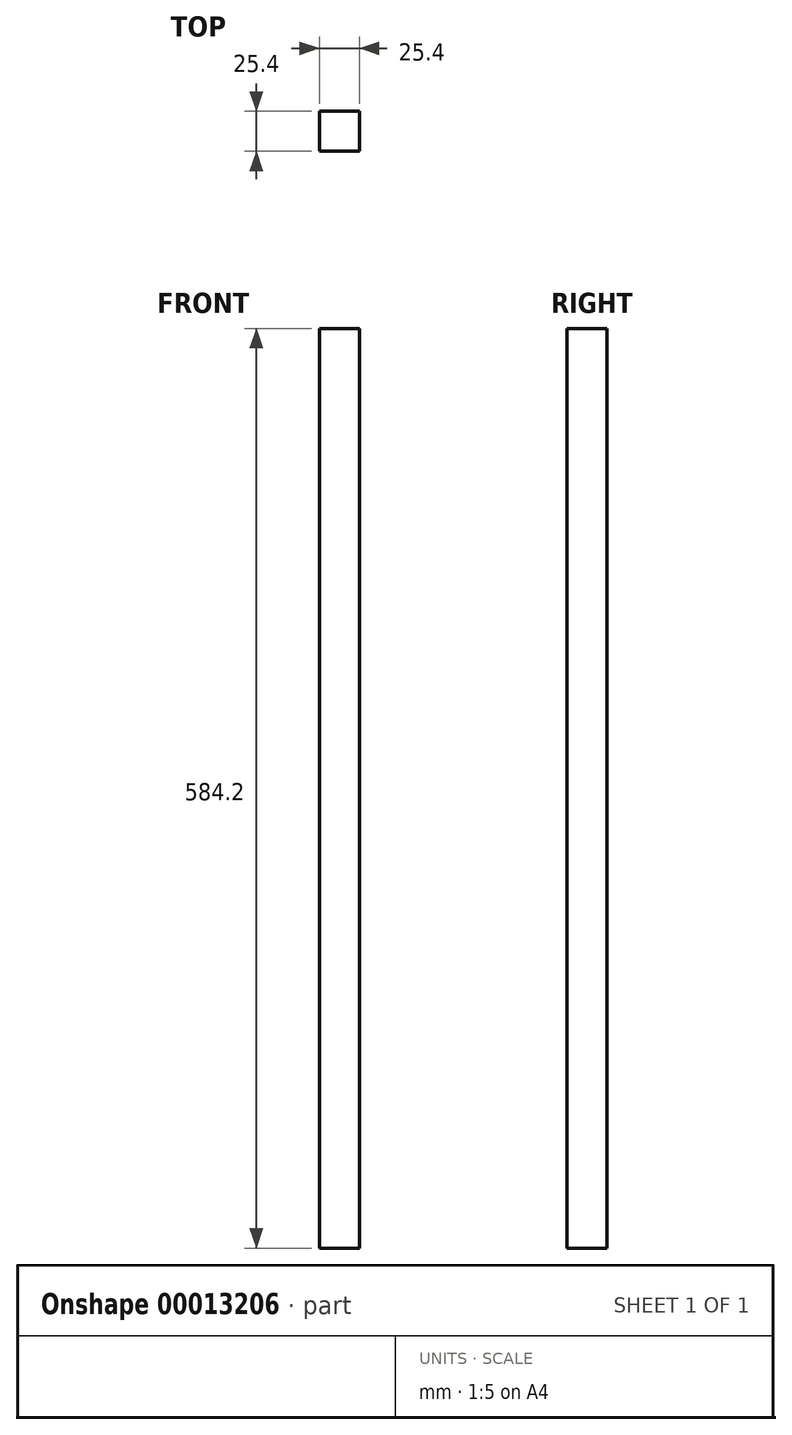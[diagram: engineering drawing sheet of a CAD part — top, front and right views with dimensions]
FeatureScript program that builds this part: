
annotation { "Feature Type Name" : "Feature", "Feature Type Description" : "" }
export const myFeature = defineFeature(function(context is Context, id is Id, definition is map)
    precondition{}
    {
        {
            var Q0;
            Q0=qCreatedBy(makeId("Top.planeOp"),FACE);
            var sketch = newSketch(context, id + "F0", { "sketchPlane" : qUnion([Q0])});
            skLineSegment(sketch, "E0.rect.bottom", {"start": v(12.7, -12.7) * mm, "end": v(-12.7, -12.7) * mm});
            skLineSegment(sketch, "E0.rect.top", {"start": v(12.7, 12.7) * mm, "end": v(-12.7, 12.7) * mm});
            skLineSegment(sketch, "E0.rect.left", {"start": v(12.7, -12.7) * mm, "end": v(12.7, 12.7) * mm});
            skLineSegment(sketch, "E0.rect.right", {"start": v(-12.7, -12.7) * mm, "end": v(-12.7, 12.7) * mm});
            skPoint(sketch, "E0.rect.middle", {"position": v(0, 0) * mm});
            skSolve(sketch);
        }
        {
            var Q0;
            Q0 = qSketchRegion(id + "F0", true);
            extrude(context, id + "F1", {"entities" : qUnion([Q0]), "depth" : 584.2 * mm});
        }
    });
